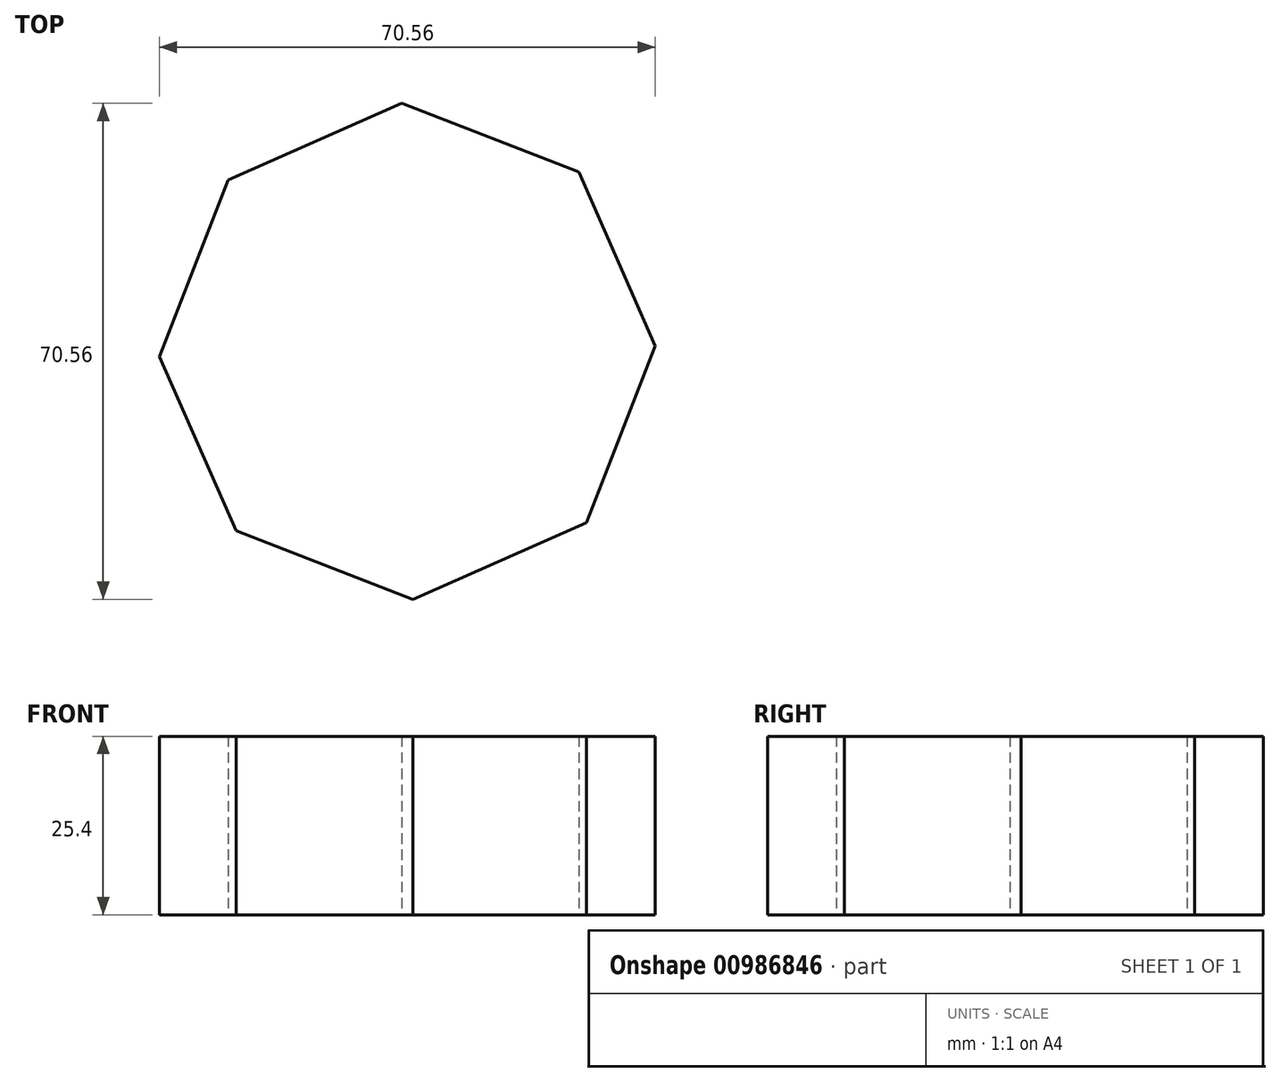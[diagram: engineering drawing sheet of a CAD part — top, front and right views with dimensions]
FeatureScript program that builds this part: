
annotation { "Feature Type Name" : "Feature", "Feature Type Description" : "" }
export const myFeature = defineFeature(function(context is Context, id is Id, definition is map)
    precondition{}
    {
        {
            var Q0;
            Q0=qCreatedBy(makeId("Top.planeOp"),FACE);
            var sketch = newSketch(context, id + "F0", { "sketchPlane" : qUnion([Q0])});
            skCircle(sketch, "E0.cCircle", {"center": v(0, 0) * mm, "radius": 32.6 * mm, "construction": true});
            skLineSegment(sketch, "E0.0", {"start": v(35.28, 0.79) * mm, "end": v(25.5, -24.39) * mm});
            skLineSegment(sketch, "E0.1", {"start": v(25.5, -24.39) * mm, "end": v(0.79, -35.28) * mm});
            skLineSegment(sketch, "E0.2", {"start": v(0.79, -35.28) * mm, "end": v(-24.39, -25.5) * mm});
            skLineSegment(sketch, "E0.3", {"start": v(-24.39, -25.5) * mm, "end": v(-35.28, -0.79) * mm});
            skLineSegment(sketch, "E0.4", {"start": v(-35.28, -0.79) * mm, "end": v(-25.5, 24.39) * mm});
            skLineSegment(sketch, "E0.5", {"start": v(-25.5, 24.39) * mm, "end": v(-0.79, 35.28) * mm});
            skLineSegment(sketch, "E0.6", {"start": v(-0.79, 35.28) * mm, "end": v(24.39, 25.5) * mm});
            skLineSegment(sketch, "E0.7", {"start": v(24.39, 25.5) * mm, "end": v(35.28, 0.79) * mm});
            skPoint(sketch, "E0.0.midPoint", {"position": v(30.4, -11.8) * mm});
            skSolve(sketch);
        }
        {
            var Q0;
            Q0=makeQuery(id+"F0.imprint","IMPRINT",FACE,{"disambiguationData":[TD([[makeQuery(id+"F0.imprint","IMPRINT",EDGE,{"derivedFrom":sQuery(id+"F0.wireOp",EDGE,"E0.0")}),-1.0]])]});
            extrude(context, id + "F1", {"entities" : qUnion([Q0]), "depth" : 25.4 * mm, "offsetDistance" : 25.4 * mm});
        }
    });
